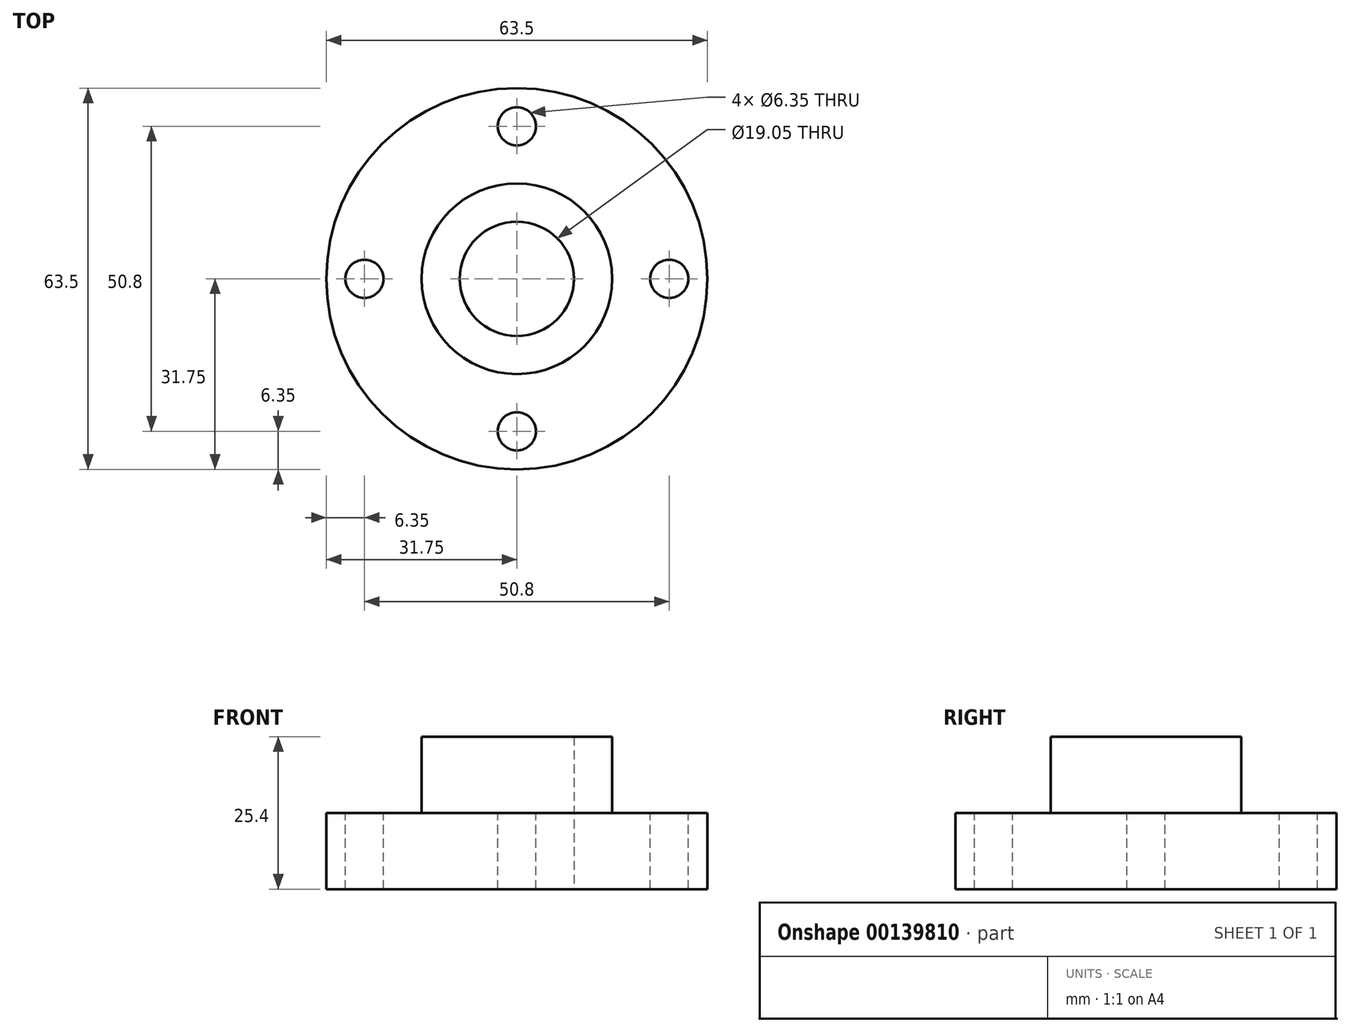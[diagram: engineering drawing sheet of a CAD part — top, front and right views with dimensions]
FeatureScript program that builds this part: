
annotation { "Feature Type Name" : "Feature", "Feature Type Description" : "" }
export const myFeature = defineFeature(function(context is Context, id is Id, definition is map)
    precondition{}
    {
        {
            var Q0;
            Q0=qCreatedBy(makeId("Top.planeOp"),FACE);
            var sketch = newSketch(context, id + "F0", { "sketchPlane" : qUnion([Q0])});
            skCircle(sketch, "E0", {"center": v(0, 0) * mm, "radius": 31.75 * mm});
            skCircle(sketch, "E1", {"center": v(0, 0) * mm, "radius": 9.53 * mm});
            skSolve(sketch);
        }
        {
            var Q0;
            Q0 = qSketchRegion(id + "F0", true);
            extrude(context, id + "F1", {"entities" : qUnion([Q0]), "depth" : 12.7 * mm});
        }
        {
            var Q0;
            Q0=makeQuery(id+"F1.opExtrude","CAP_FACE",FACE,{"disambiguationData":[OSD([sQuery(id+"F0.wireOp",EDGE,"E0"),sQuery(id+"F0.wireOp",EDGE,"E1")])],"isStart":false});
            var sketch = newSketch(context, id + "F2", { "sketchPlane" : qUnion([Q0])});
            skCircle(sketch, "E2", {"center": v(0, 0) * mm, "radius": 9.53 * mm});
            skCircle(sketch, "E3", {"center": v(0, 0) * mm, "radius": 15.88 * mm});
            skSolve(sketch);
        }
        {
            var Q0;
            Q0 = qSketchRegion(id + "F2", true);
            extrude(context, id + "F3", {"entities" : qUnion([Q0]), "operationType" : NewBodyOperationType.ADD, "depth" : 12.7 * mm});
        }
        {
            var Q0;
            Q0=makeQuery(id+"F1.opExtrude","CAP_FACE",FACE,{"disambiguationData":[OSD([sQuery(id+"F0.wireOp",EDGE,"E0"),sQuery(id+"F0.wireOp",EDGE,"E1")])],"isStart":false});
            var sketch = newSketch(context, id + "F4", { "sketchPlane" : qUnion([Q0])});
            skLineSegment(sketch, "E4", {"start": v(0, 0) * mm, "end": v(-25.4, 0) * mm, "construction": true});
            skCircle(sketch, "E5", {"center": v(-25.4, 0) * mm, "radius": 3.18 * mm});
            skCircle(sketch, "E6.1.0", {"center": v(0, -25.4) * mm, "radius": 3.18 * mm});
            skCircle(sketch, "E6.2.0", {"center": v(25.4, 0) * mm, "radius": 3.18 * mm});
            skCircle(sketch, "E6.3.0", {"center": v(0, 25.4) * mm, "radius": 3.18 * mm});
            skPoint(sketch, "E6.center", {"position": v(0, 0) * mm});
            skSolve(sketch);
        }
        {
            var Q0;
            Q0 = qSketchRegion(id + "F4", true);
            var Q1;
            Q1=makeQuery(id+"F1.opExtrude","CAP_FACE",FACE,{"disambiguationData":[OSD([sQuery(id+"F0.wireOp",EDGE,"E0"),sQuery(id+"F0.wireOp",EDGE,"E1")])],"isStart":true});
            extrude(context, id + "F5", {"entities" : qUnion([Q0]), "operationType" : NewBodyOperationType.REMOVE, "endBound" : BoundingType.UP_TO_SURFACE, "oppositeDirection" : true, "endBoundEntityFace" : qUnion([Q1]), "depth" : 25.4 * mm});
        }
    });
